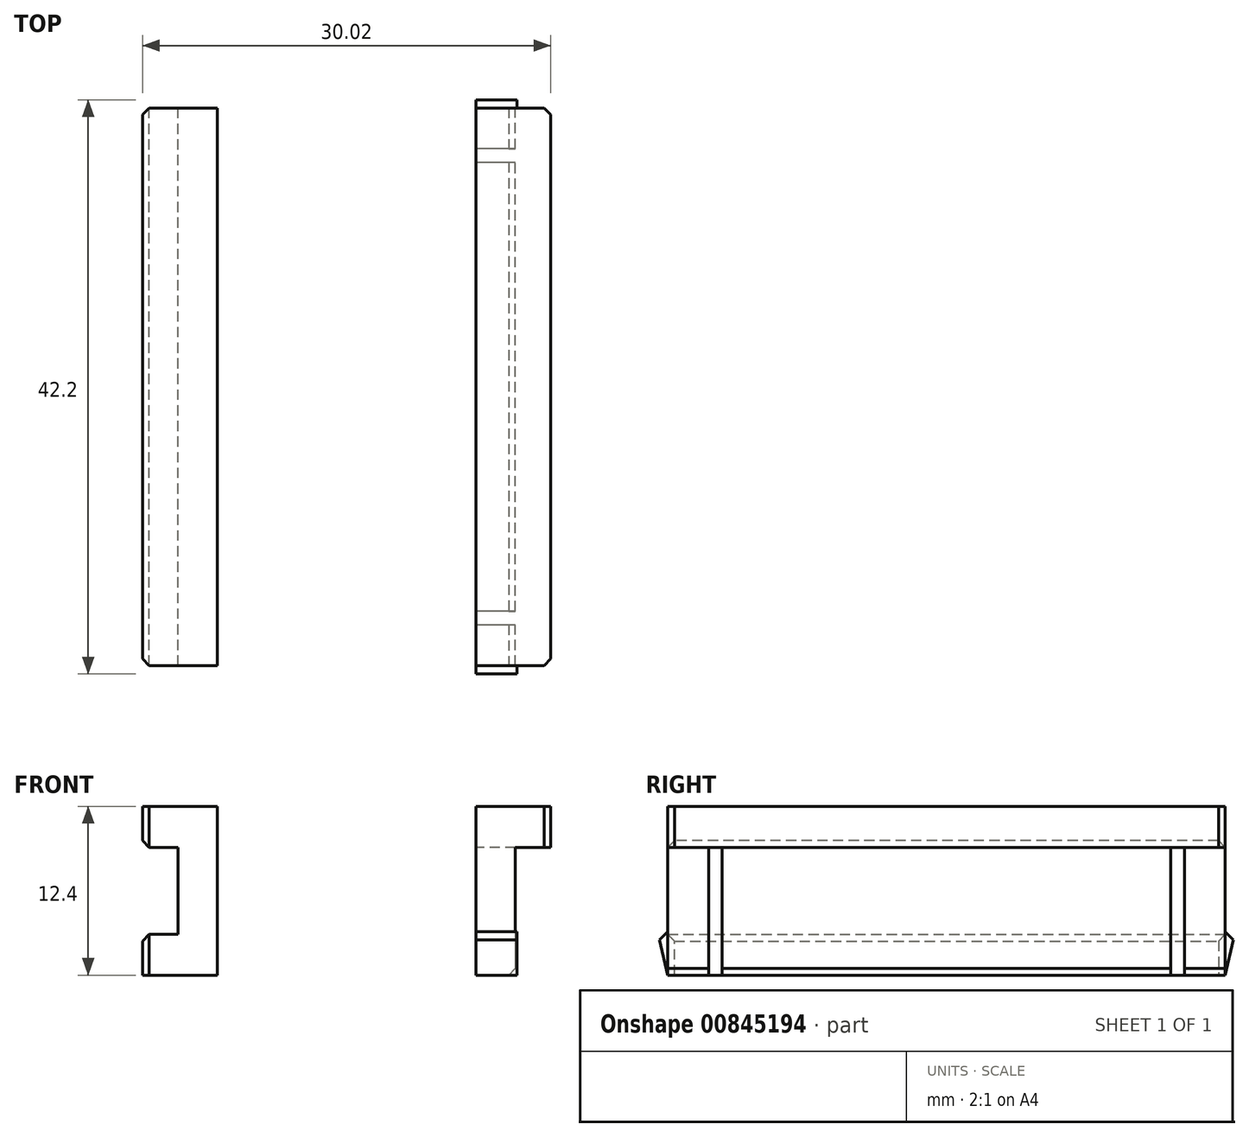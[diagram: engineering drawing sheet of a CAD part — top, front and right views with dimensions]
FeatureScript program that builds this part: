
annotation { "Feature Type Name" : "Feature", "Feature Type Description" : "" }
export const myFeature = defineFeature(function(context is Context, id is Id, definition is map)
    precondition{}
    {
        {
            var Q0;
            Q0=qCreatedBy(makeId("Front.planeOp"),FACE);
            var sketch = newSketch(context, id + "F0", { "sketchPlane" : qUnion([Q0])});
            skLineSegment(sketch, "E0.bottom", {"start": v(0, 0) * mm, "end": v(2.9, 0) * mm});
            skLineSegment(sketch, "E0.top", {"start": v(0, -12.4) * mm, "end": v(2.9, -12.4) * mm});
            skLineSegment(sketch, "E0.left", {"start": v(0, 0) * mm, "end": v(0, -12.4) * mm});
            skLineSegment(sketch, "E0.right", {"start": v(2.9, 0) * mm, "end": v(2.9, -12.4) * mm});
            skLineSegment(sketch, "E1.bottom", {"start": v(0, -12.4) * mm, "end": v(-2.6, -12.4) * mm});
            skLineSegment(sketch, "E1.top", {"start": v(0, -9.4) * mm, "end": v(-2.6, -9.4) * mm});
            skLineSegment(sketch, "E1.left", {"start": v(0, -12.4) * mm, "end": v(0, -9.4) * mm});
            skLineSegment(sketch, "E1.right", {"start": v(-2.6, -12.4) * mm, "end": v(-2.6, -9.4) * mm});
            skLineSegment(sketch, "E2.bottom", {"start": v(0, 0) * mm, "end": v(-2.6, 0) * mm});
            skLineSegment(sketch, "E2.top", {"start": v(0, -3) * mm, "end": v(-2.6, -3) * mm});
            skLineSegment(sketch, "E2.left", {"start": v(0, 0) * mm, "end": v(0, -3) * mm});
            skLineSegment(sketch, "E2.right", {"start": v(-2.6, 0) * mm, "end": v(-2.6, -3) * mm});
            skLineSegment(sketch, "E3.bottom", {"start": v(21.92, 0) * mm, "end": v(24.82, 0) * mm});
            skLineSegment(sketch, "E3.top", {"start": v(21.92, -12.4) * mm, "end": v(24.82, -12.4) * mm});
            skLineSegment(sketch, "E3.left", {"start": v(21.92, 0) * mm, "end": v(21.92, -12.4) * mm});
            skLineSegment(sketch, "E3.right", {"start": v(24.82, 0) * mm, "end": v(24.82, -12.4) * mm});
            skLineSegment(sketch, "E4.bottom", {"start": v(24.82, 0) * mm, "end": v(27.42, 0) * mm});
            skLineSegment(sketch, "E4.top", {"start": v(24.82, -3) * mm, "end": v(27.42, -3) * mm});
            skLineSegment(sketch, "E4.left", {"start": v(24.82, 0) * mm, "end": v(24.82, -3) * mm});
            skLineSegment(sketch, "E4.right", {"start": v(27.42, 0) * mm, "end": v(27.42, -3) * mm});
            skLineSegment(sketch, "E5", {"start": v(-5.45, -9.4) * mm, "end": v(29.2, -9.4) * mm, "construction": true});
            skSolve(sketch);
        }
        {
            var Q0;
            Q0=makeQuery(id+"F0.imprint","IMPRINT",FACE,{"disambiguationData":[TD([[makeQuery(id+"F0.imprint","IMPRINT",EDGE,{"derivedFrom":sQuery(id+"F0.wireOp",EDGE,"E0.bottom")}),-1.0]])]});
            var Q1;
            Q1=makeQuery(id+"F0.imprint","IMPRINT",FACE,{"disambiguationData":[TD([[makeQuery(id+"F0.imprint","IMPRINT",EDGE,{"derivedFrom":sQuery(id+"F0.wireOp",EDGE,"E1.bottom")}),-1.0]])]});
            var Q2;
            Q2=makeQuery(id+"F0.imprint","IMPRINT",FACE,{"disambiguationData":[TD([[makeQuery(id+"F0.imprint","IMPRINT",EDGE,{"derivedFrom":sQuery(id+"F0.wireOp",EDGE,"E2.bottom")}),1.0]])]});
            var Q3;
            Q3=makeQuery(id+"F0.imprint","IMPRINT",FACE,{"disambiguationData":[TD([[makeQuery(id+"F0.imprint","IMPRINT",EDGE,{"derivedFrom":sQuery(id+"F0.wireOp",EDGE,"E3.bottom")}),-1.0]])]});
            var Q4;
            Q4=makeQuery(id+"F0.imprint","IMPRINT",FACE,{"disambiguationData":[TD([[makeQuery(id+"F0.imprint","IMPRINT",EDGE,{"derivedFrom":sQuery(id+"F0.wireOp",EDGE,"E4.bottom")}),-1.0]])]});
            extrude(context, id + "F1", {"entities" : qUnion([Q0, Q1, Q2, Q3, Q4]), "depth" : 41 * mm, "offsetDistance" : 25 * mm});
        }
        {
            var Q0;
            Q0=makeQuery(id+"F1.opExtrude","SWEPT_FACE",FACE,{"disambiguationData":[OSD([sQuery(id+"F0.wireOp",EDGE,"E3.left")])]});
            var sketch = newSketch(context, id + "F2", { "sketchPlane" : qUnion([Q0])});
            skLineSegment(sketch, "E6.bottom", {"start": v(38, -12.4) * mm, "end": v(37, -12.4) * mm});
            skLineSegment(sketch, "E6.top", {"start": v(38, -3) * mm, "end": v(37, -3) * mm});
            skLineSegment(sketch, "E6.left", {"start": v(38, -12.4) * mm, "end": v(38, -3) * mm});
            skLineSegment(sketch, "E6.right", {"start": v(37, -12.4) * mm, "end": v(37, -3) * mm});
            skLineSegment(sketch, "E7.bottom", {"start": v(4, -12.4) * mm, "end": v(3, -12.4) * mm});
            skLineSegment(sketch, "E7.top", {"start": v(4, -3) * mm, "end": v(3, -3) * mm});
            skLineSegment(sketch, "E7.left", {"start": v(4, -12.4) * mm, "end": v(4, -3) * mm});
            skLineSegment(sketch, "E7.right", {"start": v(3, -12.4) * mm, "end": v(3, -3) * mm});
            skLineSegment(sketch, "E8", {"start": v(41, -9.2) * mm, "end": v(0, -9.2) * mm, "construction": true});
            skLineSegment(sketch, "E9", {"start": v(0, -9.2) * mm, "end": v(-0.6, -9.8) * mm});
            skLineSegment(sketch, "E10", {"start": v(-0.6, -9.8) * mm, "end": v(0, -12.4) * mm});
            skLineSegment(sketch, "E11", {"start": v(41, -9.2) * mm, "end": v(41.6, -9.8) * mm});
            skLineSegment(sketch, "E12", {"start": v(41.6, -9.8) * mm, "end": v(41, -12.4) * mm});
            skLineSegment(sketch, "E13", {"start": v(43.47, -9.8) * mm, "end": v(-2.3, -9.8) * mm, "construction": true});
            skLineSegment(sketch, "E14", {"start": v(42.43, -3) * mm, "end": v(-2.03, -3) * mm, "construction": true});
            skLineSegment(sketch, "E15.0", {"start": v(41, -9.4) * mm, "end": v(0, -9.4) * mm});
            skSolve(sketch);
        }
        {
            var Q0;
            {var subQ0=sQuery(id+"F2.wireOp",EDGE,"E6.bottom");Q0=makeQuery(id+"F2.imprint","IMPRINT",FACE,{"disambiguationData":[TD([[makeQuery(id+"F2.imprint","IMPRINT",EDGE,{"derivedFrom":subQ0}),-1.0]])]});}
            var Q1;
            {var subQ0=sQuery(id+"F2.wireOp",EDGE,"E6.top");Q1=makeQuery(id+"F2.imprint","IMPRINT",FACE,{"disambiguationData":[TD([[makeQuery(id+"F2.imprint","IMPRINT",EDGE,{"derivedFrom":subQ0}),1.0]])]});}
            var Q2;
            {var subQ0=sQuery(id+"F2.wireOp",EDGE,"E7.bottom");Q2=makeQuery(id+"F2.imprint","IMPRINT",FACE,{"disambiguationData":[TD([[makeQuery(id+"F2.imprint","IMPRINT",EDGE,{"derivedFrom":subQ0}),-1.0]])]});}
            var Q3;
            {var subQ0=sQuery(id+"F2.wireOp",EDGE,"E7.top");Q3=makeQuery(id+"F2.imprint","IMPRINT",FACE,{"disambiguationData":[TD([[makeQuery(id+"F2.imprint","IMPRINT",EDGE,{"derivedFrom":subQ0}),1.0]])]});}
            extrude(context, id + "F3", {"entities" : qUnion([Q0, Q1, Q2, Q3]), "operationType" : NewBodyOperationType.REMOVE, "oppositeDirection" : true, "depth" : 3 * mm, "offsetDistance" : 25 * mm});
        }
        {
            var Q0;
            {var subQ0=sQuery(id+"F2.wireOp",EDGE,"E11");Q0=makeQuery(id+"F2.imprint","IMPRINT",FACE,{"disambiguationData":[TD([[makeQuery(id+"F2.imprint","IMPRINT",EDGE,{"derivedFrom":subQ0}),-1.0]])]});}
            var Q1;
            {var subQ0=sQuery(id+"F2.wireOp",EDGE,"E9");Q1=makeQuery(id+"F2.imprint","IMPRINT",FACE,{"disambiguationData":[TD([[makeQuery(id+"F2.imprint","IMPRINT",EDGE,{"derivedFrom":subQ0}),1.0]])]});}
            extrude(context, id + "F4", {"entities" : qUnion([Q0, Q1]), "oppositeDirection" : true, "depth" : 3 * mm, "offsetDistance" : 25 * mm});
        }
        {
            var Q0;
            Q0=makeQuery(id+"F1.opExtrude","SWEPT_EDGE",EDGE,{"disambiguationData":[OSD([sQuery(id+"F0.wireOp",EDGE,"E2.top"),sQuery(id+"F0.wireOp",EDGE,"E2.right")])]});
            var Q1;
            Q1=makeQuery(id+"F1.opExtrude","SWEPT_EDGE",EDGE,{"disambiguationData":[OSD([sQuery(id+"F0.wireOp",EDGE,"E1.top"),sQuery(id+"F0.wireOp",EDGE,"E1.right")])]});
            var Q2;
            Q2=makeQuery(id+"F1.opExtrude","CAP_EDGE",EDGE,{"disambiguationData":[OSD([sQuery(id+"F0.wireOp",EDGE,"E2.right")])],"isStart":false});
            var Q3;
            Q3=makeQuery(id+"F1.opExtrude","CAP_EDGE",EDGE,{"disambiguationData":[OSD([sQuery(id+"F0.wireOp",EDGE,"E1.right")])],"isStart":false});
            var Q4;
            Q4=makeQuery(id+"F1.opExtrude","CAP_EDGE",EDGE,{"disambiguationData":[OSD([sQuery(id+"F0.wireOp",EDGE,"E1.right")])],"isStart":true});
            var Q5;
            Q5=makeQuery(id+"F1.opExtrude","CAP_EDGE",EDGE,{"disambiguationData":[OSD([sQuery(id+"F0.wireOp",EDGE,"E2.right")])],"isStart":true});
            chamfer(context, id + "F5", {"entities" : qUnion([Q0, Q1, Q2, Q3, Q4, Q5]), "width" : 0.5 * mm, "tangentPropagation" : true});
        }
        {
            var Q0;
            {var subQ0=sQuery(id+"F0.wireOp",EDGE,"E3.top");var subQ1=sQuery(id+"F0.wireOp",EDGE,"E3.right");Q0=makeQuery(id+"F3.boolean.opBoolean","SPLIT",EDGE,{"disambiguationData":[TD([makeQuery(id+"F3.opExtrude","SWEPT_FACE",FACE,{"disambiguationData":[OSD([sQuery(id+"F2.wireOp",EDGE,"E6.right")])]})])],"derivedFrom":makeQuery(id+"F1.opExtrude","SWEPT_EDGE",EDGE,{"disambiguationData":[OSD([subQ0,subQ1])]})});}
            var Q1;
            {var subQ0=sQuery(id+"F0.wireOp",EDGE,"E3.right");var subQ1=sQuery(id+"F0.wireOp",EDGE,"E3.top");Q1=makeQuery(id+"F3.boolean.opBoolean","SPLIT",EDGE,{"disambiguationData":[TD([makeQuery(id+"F3.opExtrude","SWEPT_FACE",FACE,{"disambiguationData":[OSD([sQuery(id+"F2.wireOp",EDGE,"E6.left")])]})])],"derivedFrom":makeQuery(id+"F1.opExtrude","SWEPT_EDGE",EDGE,{"disambiguationData":[OSD([subQ1,subQ0])]})});}
            var Q2;
            {var subQ0=sQuery(id+"F0.wireOp",EDGE,"E3.right");var subQ1=sQuery(id+"F0.wireOp",EDGE,"E3.top");Q2=makeQuery(id+"F3.boolean.opBoolean","SPLIT",EDGE,{"disambiguationData":[TD([makeQuery(id+"F3.opExtrude","SWEPT_FACE",FACE,{"disambiguationData":[OSD([sQuery(id+"F2.wireOp",EDGE,"E7.right")])]})])],"derivedFrom":makeQuery(id+"F1.opExtrude","SWEPT_EDGE",EDGE,{"disambiguationData":[OSD([subQ1,subQ0])]})});}
            var Q3;
            Q3=makeQuery(id+"F1.opExtrude","CAP_EDGE",EDGE,{"disambiguationData":[OSD([sQuery(id+"F0.wireOp",EDGE,"E4.right")])],"isStart":false});
            var Q4;
            Q4=makeQuery(id+"F1.opExtrude","CAP_EDGE",EDGE,{"disambiguationData":[OSD([sQuery(id+"F0.wireOp",EDGE,"E4.right")])],"isStart":true});
            chamfer(context, id + "F6", {"entities" : qUnion([Q0, Q1, Q2, Q3, Q4]), "width" : 0.5 * mm, "tangentPropagation" : true});
        }
    });
